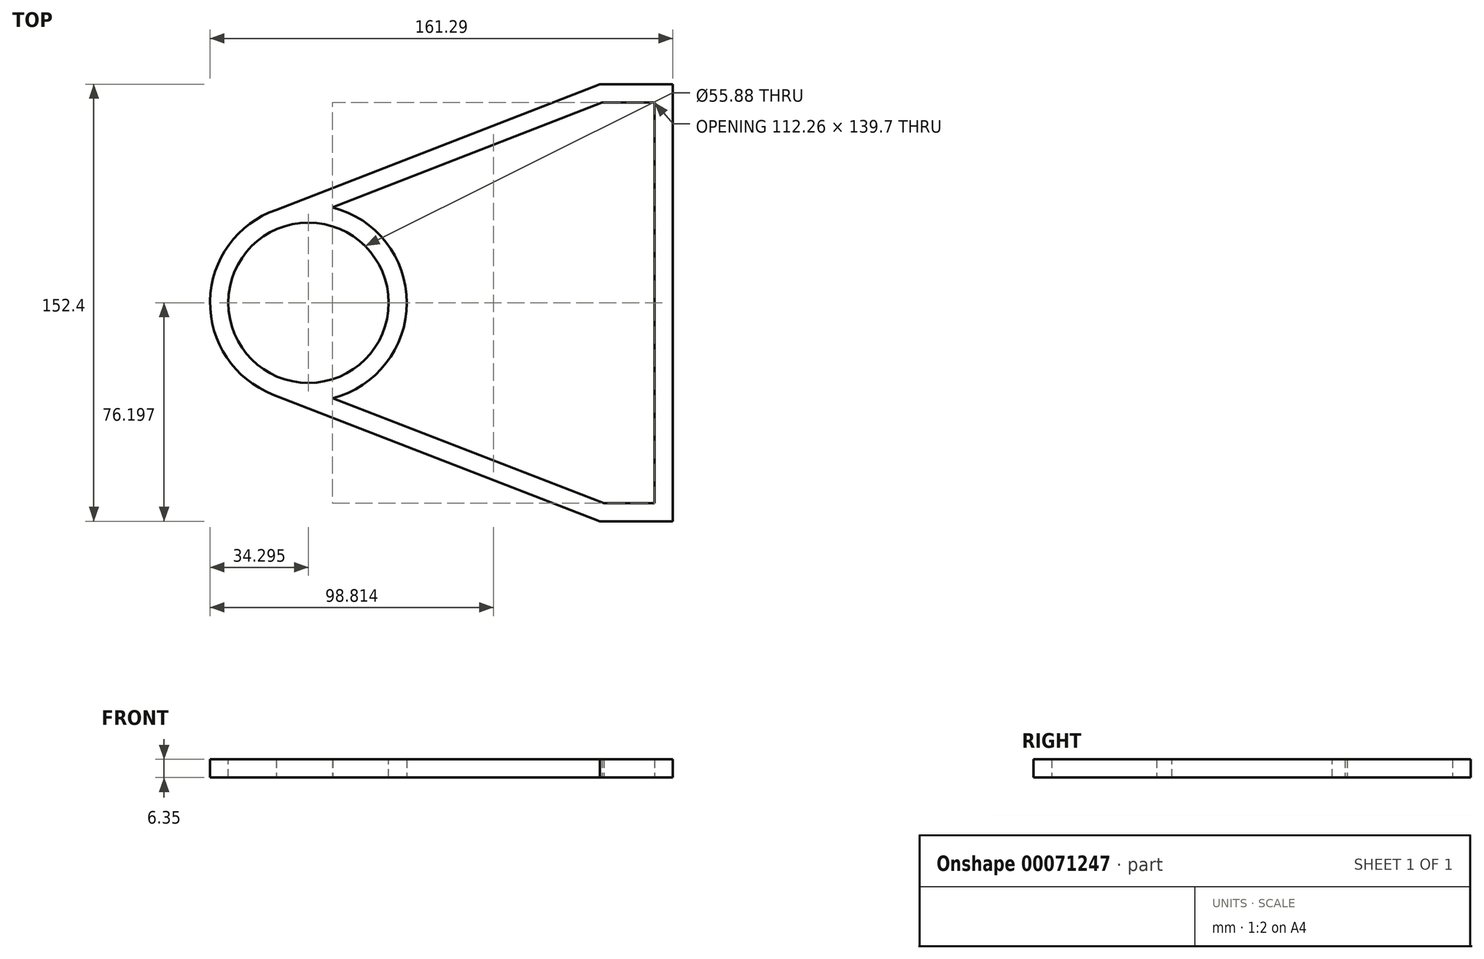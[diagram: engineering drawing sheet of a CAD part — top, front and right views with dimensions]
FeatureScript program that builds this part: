
annotation { "Feature Type Name" : "Feature", "Feature Type Description" : "" }
export const myFeature = defineFeature(function(context is Context, id is Id, definition is map)
    precondition{}
    {
        {
            var Q0;
            Q0=qCreatedBy(makeId("Top.planeOp"),FACE);
            var sketch = newSketch(context, id + "F0", { "sketchPlane" : qUnion([Q0])});
            skLineSegment(sketch, "E0", {"start": v(69.82, 65.3) * mm, "end": v(69.82, -87.1) * mm});
            skLineSegment(sketch, "E1", {"start": v(69.82, -87.1) * mm, "end": v(44.42, -87.1) * mm});
            skLineSegment(sketch, "E2", {"start": v(44.42, -87.1) * mm, "end": v(-69.58, -42.86) * mm});
            skLineSegment(sketch, "E3", {"start": v(69.82, 65.3) * mm, "end": v(44.42, 65.3) * mm});
            skLineSegment(sketch, "E4", {"start": v(44.42, 65.3) * mm, "end": v(-68.38, 21.52) * mm});
            skArc(sketch, "E5", {"start": v(-69.58, -42.86) * mm, "mid": v(-91.46, -10.25) * mm, "end": v(-68.38, 21.52) * mm});
            skLineSegment(sketch, "E6", {"start": v(69.82, -10.9) * mm, "end": v(-57.18, -10.9) * mm});
            skLineSegment(sketch, "E7.0", {"start": v(63.47, 65.3) * mm, "end": v(63.47, -87.1) * mm});
            skLineSegment(sketch, "E8.0", {"start": v(69.82, -80.74) * mm, "end": v(44.42, -80.74) * mm});
            skLineSegment(sketch, "E9.0", {"start": v(69.82, 58.96) * mm, "end": v(44.42, 58.96) * mm});
            skLineSegment(sketch, "E10.0", {"start": v(46.72, 59.39) * mm, "end": v(-66.08, 15.6) * mm});
            skSolve(sketch);
        }
        {
            var Q0;
            Q0 = qSketchRegion(id + "F0", true);
            extrude(context, id + "F1", {"entities" : qUnion([Q0]), "depth" : 6.35 * mm});
        }
        {
            var Q0;
            Q0=makeQuery(id+"F1.opExtrude","CAP_FACE",FACE,{"disambiguationData":[OSD([sQuery(id+"F0.wireOp",EDGE,"E0"),sQuery(id+"F0.wireOp",EDGE,"E1"),sQuery(id+"F0.wireOp",EDGE,"E2"),sQuery(id+"F0.wireOp",EDGE,"E3"),sQuery(id+"F0.wireOp",EDGE,"E4"),sQuery(id+"F0.wireOp",EDGE,"E5")])],"isStart":false});
            var sketch = newSketch(context, id + "F2", { "sketchPlane" : qUnion([Q0])});
            skCircle(sketch, "E11", {"center": v(-57.18, -10.9) * mm, "radius": 27.94 * mm});
            skSolve(sketch);
        }
        {
            var Q0;
            Q0 = qSketchRegion(id + "F2", true);
            extrude(context, id + "F3", {"entities" : qUnion([Q0]), "operationType" : NewBodyOperationType.REMOVE, "oppositeDirection" : true, "depth" : 25.4 * mm});
        }
        {
            var Q0;
            Q0=qCreatedBy(makeId("Top.planeOp"),FACE);
            var sketch = newSketch(context, id + "F4", { "sketchPlane" : qUnion([Q0])});
            skLineSegment(sketch, "E12.0", {"start": v(63.47, 58.96) * mm, "end": v(63.47, -80.74) * mm});
            skLineSegment(sketch, "E13.0", {"start": v(63.47, -80.74) * mm, "end": v(45.78, -80.74) * mm});
            skLineSegment(sketch, "E14.0", {"start": v(63.47, 58.96) * mm, "end": v(45.24, 58.96) * mm});
            skArc(sketch, "E15.0", {"start": v(-69.61, 21.06) * mm, "mid": v(-91.47, -10.92) * mm, "end": v(-69.56, -42.87) * mm});
            skLineSegment(sketch, "E16", {"start": v(44.64, 65.54) * mm, "end": v(-69.61, 21.06) * mm});
            skLineSegment(sketch, "E17.0", {"start": v(45.24, 58.96) * mm, "end": v(-48.79, 22.36) * mm});
            skLineSegment(sketch, "E18", {"start": v(44.68, -87.12) * mm, "end": v(-69.56, -42.87) * mm});
            skLineSegment(sketch, "E19.0", {"start": v(45.78, -80.74) * mm, "end": v(-48.73, -44.13) * mm});
            skArc(sketch, "E20.trimOffspring", {"start": v(-48.73, -44.13) * mm, "mid": v(-22.89, -10.86) * mm, "end": v(-48.79, 22.36) * mm});
            skSolve(sketch);
        }
        {
            var Q0;
            Q0 = qSketchRegion(id + "F4", true);
            extrude(context, id + "F5", {"entities" : qUnion([Q0]), "operationType" : NewBodyOperationType.REMOVE, "depth" : 25.4 * mm});
        }
    });
